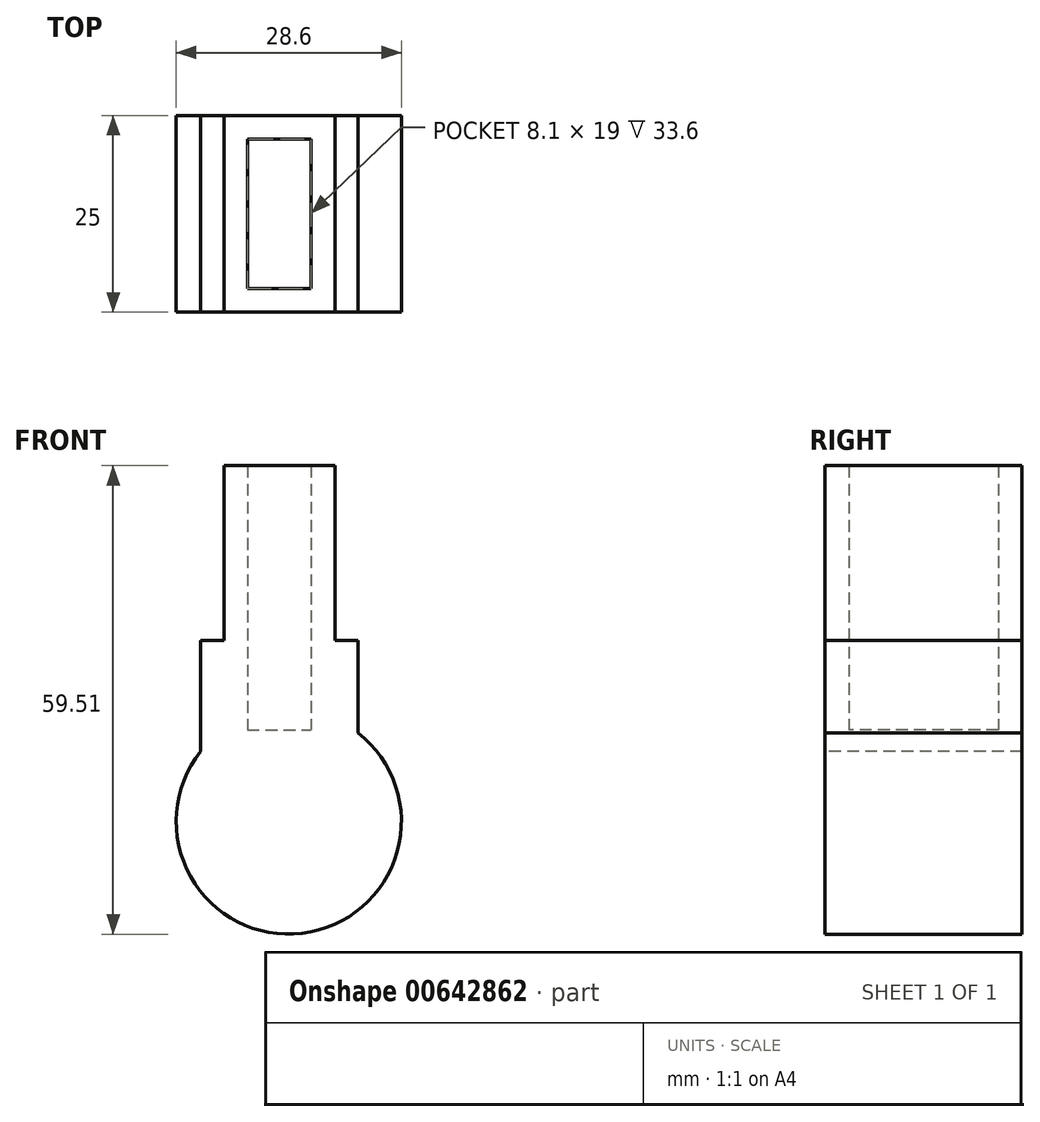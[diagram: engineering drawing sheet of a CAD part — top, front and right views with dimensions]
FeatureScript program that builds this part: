
annotation { "Feature Type Name" : "Feature", "Feature Type Description" : "" }
export const myFeature = defineFeature(function(context is Context, id is Id, definition is map)
    precondition{}
    {
        {
            var Q0;
            Q0=qCreatedBy(makeId("Front.planeOp"),FACE);
            var sketch = newSketch(context, id + "F0", { "sketchPlane" : qUnion([Q0])});
            skLineSegment(sketch, "E0.bottom", {"start": v(-11.2, 11.4) * mm, "end": v(8.8, 11.4) * mm});
            skLineSegment(sketch, "E0.top", {"start": v(-11.2, -8.6) * mm, "end": v(8.8, -8.6) * mm});
            skLineSegment(sketch, "E0.left", {"start": v(-11.2, 11.4) * mm, "end": v(-11.2, -8.6) * mm});
            skLineSegment(sketch, "E0.right", {"start": v(8.8, 11.4) * mm, "end": v(8.8, -8.6) * mm});
            skSolve(sketch);
        }
        {
            var Q0;
            Q0=qCreatedBy(makeId("Front.planeOp"),FACE);
            var sketch = newSketch(context, id + "F1", { "sketchPlane" : qUnion([Q0])});
            skLineSegment(sketch, "E1.bottom", {"start": v(5.85, -5.64) * mm, "end": v(-8.25, -5.64) * mm});
            skLineSegment(sketch, "E1.top", {"start": v(5.85, 33.6) * mm, "end": v(-8.25, 33.6) * mm});
            skLineSegment(sketch, "E1.left", {"start": v(5.85, -5.64) * mm, "end": v(5.85, 33.6) * mm});
            skLineSegment(sketch, "E1.right", {"start": v(-8.25, -5.64) * mm, "end": v(-8.25, 33.6) * mm});
            skSolve(sketch);
        }
        {
            var Q0;
            Q0 = qSketchRegion(id + "F0", true);
            extrude(context, id + "F2", {"entities" : qUnion([Q0]), "depth" : 25 * mm, "offsetDistance" : 25 * mm});
        }
        {
            var Q0;
            Q0 = qSketchRegion(id + "F1", true);
            extrude(context, id + "F3", {"entities" : qUnion([Q0]), "operationType" : NewBodyOperationType.ADD, "depth" : 25 * mm, "offsetDistance" : 25 * mm});
        }
        {
            var Q0;
            Q0=qCreatedBy(makeId("Front.planeOp"),FACE);
            var sketch = newSketch(context, id + "F4", { "sketchPlane" : qUnion([Q0])});
            skLineSegment(sketch, "E2", {"start": v(0, 0) * mm, "end": v(0, -26.6) * mm});
            skCircle(sketch, "E3", {"center": v(0, -11.61) * mm, "radius": 14.3 * mm});
            skSolve(sketch);
        }
        {
            var Q0;
            Q0 = qSketchRegion(id + "F4", true);
            var Q1;
            Q1=makeQuery(id+"F2.opExtrude","SWEPT_EDGE",EDGE,{"disambiguationData":[OSD([sQuery(id+"F0.wireOp",EDGE,"E0.bottom"),sQuery(id+"F0.wireOp",EDGE,"E0.left")])]});
            sweep(context, id + "F5", {"operationType" : NewBodyOperationType.ADD, "profiles" : qUnion([Q0]), "path" : qUnion([Q1])});
        }
        {
            var Q0;
            Q0=qCreatedBy(makeId("Top.planeOp"),FACE);
            var sketch = newSketch(context, id + "F6", { "sketchPlane" : qUnion([Q0])});
            skLineSegment(sketch, "E4.bottom", {"start": v(-5.25, -3) * mm, "end": v(2.85, -3) * mm});
            skLineSegment(sketch, "E4.top", {"start": v(-5.25, -22) * mm, "end": v(2.85, -22) * mm});
            skLineSegment(sketch, "E4.left", {"start": v(-5.25, -3) * mm, "end": v(-5.25, -22) * mm});
            skLineSegment(sketch, "E4.right", {"start": v(2.85, -3) * mm, "end": v(2.85, -22) * mm});
            skSolve(sketch);
        }
        {
            var Q0;
            Q0 = qSketchRegion(id + "F6", true);
            extrude(context, id + "F7", {"entities" : qUnion([Q0]), "operationType" : NewBodyOperationType.REMOVE, "endBound" : BoundingType.THROUGH_ALL, "depth" : 80 * mm, "offsetDistance" : 25 * mm});
        }
    });
